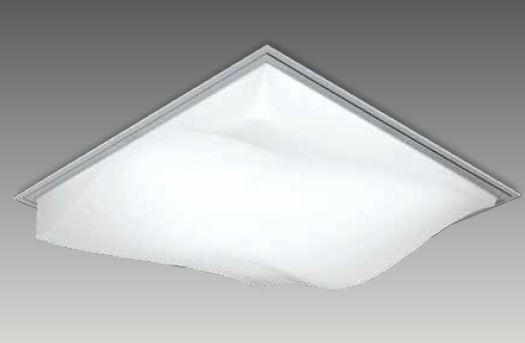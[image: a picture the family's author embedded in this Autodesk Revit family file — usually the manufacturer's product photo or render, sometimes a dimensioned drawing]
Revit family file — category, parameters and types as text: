
# Revit family: G 6060 ETR
name_source: partatom
category: Lighting Fixtures
revit_build: Autodesk Revit 2017 (Build: 20160225_1515(x64)
units: mm (PartAtom-declared; Revit-internal decimal feet)

## family parameters
Always vertical = Yes
Cut with Voids When Loaded = No
Host = Ceiling
Light Source = Yes
OmniClass Number = 23.80.70.11
OmniClass Title = Luminaries for Internal Lighting
Part Type = Normal
Room Calculation Point = No
Round Connector Dimension = Use Diameter
Shared = No

## types (4) — shared parameters
Color Filter = 16777215
Dimming Lamp Color Temperature Shift = <None>
Emit Shape Visible in Rendering = No
Emit from Rectangle Length = 550 mm  [stored 1.80446 ft]
Emit from Rectangle Width = 550 mm  [stored 1.80446 ft]
Light Source Symbol Size = 610 mm
Manufacturer = ARLIGHT
Type Image = G 6060 ETR.JPG

## per-type parameters (varying)
| type | Wattage Comments |
| GETR.6060.36.30 | 36 |
| GETR.6060.36.40 | 36 |
| GETR.6060.28.30 | 28 |
| GETR.6060.28.40 | 28 |

note: [stored X ft] marks values corroborated as IEEE doubles in the binary element streams (Revit-internal decimal feet)

## geometry (parser evidence)
native form markers: Sweep x2
no freeform markers — native parametric forms only
